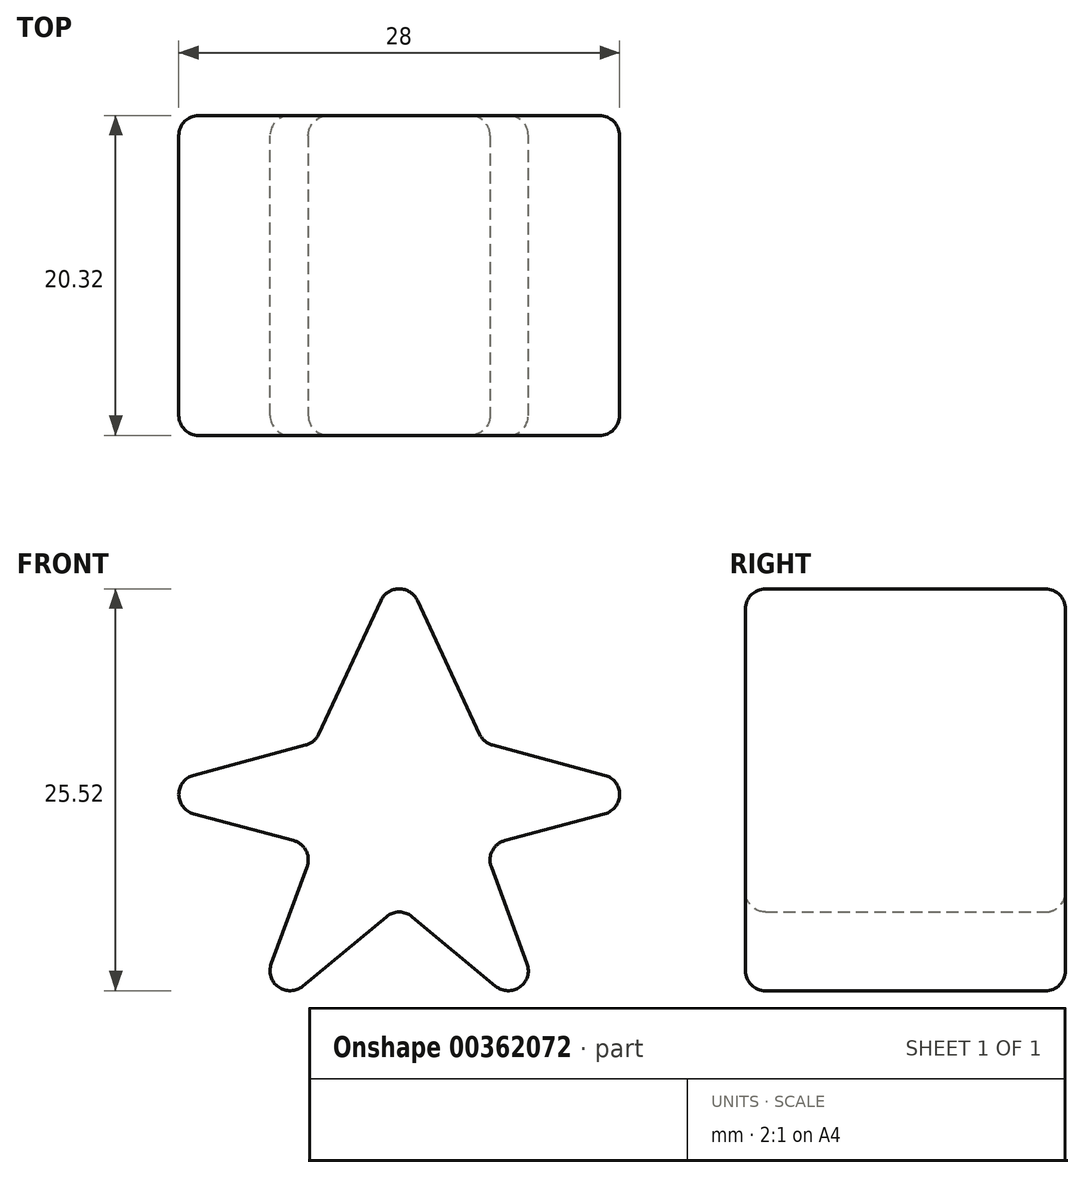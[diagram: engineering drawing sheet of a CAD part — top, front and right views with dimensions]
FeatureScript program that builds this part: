
annotation { "Feature Type Name" : "Feature", "Feature Type Description" : "" }
export const myFeature = defineFeature(function(context is Context, id is Id, definition is map)
    precondition{}
    {
        {
            var Q0;
            Q0=qCreatedBy(makeId("Front.planeOp"),FACE);
            var sketch = newSketch(context, id + "F0", { "sketchPlane" : qUnion([Q0])});
            skLineSegment(sketch, "E0", {"start": v(0, 14.8) * mm, "end": v(-5.37, 3.29) * mm});
            skLineSegment(sketch, "E1", {"start": v(-5.37, 3.29) * mm, "end": v(-17.63, 0) * mm});
            skLineSegment(sketch, "E2", {"start": v(-17.63, 0) * mm, "end": v(-5.37, -3.29) * mm});
            skLineSegment(sketch, "E3", {"start": v(-5.37, -3.29) * mm, "end": v(-9.77, -15.2) * mm});
            skLineSegment(sketch, "E4", {"start": v(-9.77, -15.2) * mm, "end": v(0, -7.08) * mm});
            skLineSegment(sketch, "E5.MirrorCS", {"start": v(0, 14.8) * mm, "end": v(5.37, 3.29) * mm});
            skLineSegment(sketch, "E6.MirrorCS", {"start": v(5.37, 3.29) * mm, "end": v(17.63, 0) * mm});
            skLineSegment(sketch, "E7.MirrorCS", {"start": v(17.63, 0) * mm, "end": v(5.37, -3.29) * mm});
            skLineSegment(sketch, "E8.MirrorCS", {"start": v(5.37, -3.29) * mm, "end": v(9.77, -15.2) * mm});
            skLineSegment(sketch, "E9.MirrorCS", {"start": v(9.77, -15.2) * mm, "end": v(0, -7.08) * mm});
            skSolve(sketch);
        }
        {
            var Q0;
            Q0=makeQuery(id+"F0.imprint","IMPRINT",FACE,{"disambiguationData":[TD([[makeQuery(id+"F0.imprint","IMPRINT",EDGE,{"derivedFrom":sQuery(id+"F0.wireOp",EDGE,"E0")}),1.0]])]});
            extrude(context, id + "F1", {"entities" : qUnion([Q0]), "depth" : 20.32 * mm});
        }
        {
            var Q0;
            Q0=makeQuery(id+"F1.opExtrude","CAP_EDGE",EDGE,{"disambiguationData":[OSD([sQuery(id+"F0.wireOp",EDGE,"E2")])],"isStart":false});
            var Q1;
            Q1=makeQuery(id+"F1.opExtrude","SWEPT_EDGE",EDGE,{"disambiguationData":[OSD([sQuery(id+"F0.wireOp",EDGE,"E0"),sQuery(id+"F0.wireOp",EDGE,"E5.MirrorCS")])]});
            var Q2;
            Q2=makeQuery(id+"F1.opExtrude","SWEPT_EDGE",EDGE,{"disambiguationData":[OSD([sQuery(id+"F0.wireOp",EDGE,"E1"),sQuery(id+"F0.wireOp",EDGE,"E2")])]});
            var Q3;
            Q3=makeQuery(id+"F1.opExtrude","SWEPT_EDGE",EDGE,{"disambiguationData":[OSD([sQuery(id+"F0.wireOp",EDGE,"E6.MirrorCS"),sQuery(id+"F0.wireOp",EDGE,"E7.MirrorCS")])]});
            var Q4;
            Q4=makeQuery(id+"F1.opExtrude","SWEPT_EDGE",EDGE,{"disambiguationData":[OSD([sQuery(id+"F0.wireOp",EDGE,"E8.MirrorCS"),sQuery(id+"F0.wireOp",EDGE,"E9.MirrorCS")])]});
            var Q5;
            Q5=makeQuery(id+"F1.opExtrude","CAP_EDGE",EDGE,{"disambiguationData":[OSD([sQuery(id+"F0.wireOp",EDGE,"E0")])],"isStart":false});
            var Q6;
            Q6=makeQuery(id+"F1.opExtrude","CAP_EDGE",EDGE,{"disambiguationData":[OSD([sQuery(id+"F0.wireOp",EDGE,"E9.MirrorCS")])],"isStart":false});
            var Q7;
            Q7=makeQuery(id+"F1.opExtrude","CAP_EDGE",EDGE,{"disambiguationData":[OSD([sQuery(id+"F0.wireOp",EDGE,"E6.MirrorCS")])],"isStart":false});
            var Q8;
            Q8=makeQuery(id+"F1.opExtrude","CAP_EDGE",EDGE,{"disambiguationData":[OSD([sQuery(id+"F0.wireOp",EDGE,"E8.MirrorCS")])],"isStart":true});
            var Q9;
            Q9=makeQuery(id+"F1.opExtrude","CAP_EDGE",EDGE,{"disambiguationData":[OSD([sQuery(id+"F0.wireOp",EDGE,"E1")])],"isStart":false});
            var Q10;
            Q10=makeQuery(id+"F1.opExtrude","CAP_EDGE",EDGE,{"disambiguationData":[OSD([sQuery(id+"F0.wireOp",EDGE,"E2")])],"isStart":true});
            var Q11;
            Q11=makeQuery(id+"F1.opExtrude","SWEPT_EDGE",EDGE,{"disambiguationData":[OSD([sQuery(id+"F0.wireOp",EDGE,"E0"),sQuery(id+"F0.wireOp",EDGE,"E1")])]});
            var Q12;
            Q12=makeQuery(id+"F1.opExtrude","SWEPT_EDGE",EDGE,{"disambiguationData":[OSD([sQuery(id+"F0.wireOp",EDGE,"E2"),sQuery(id+"F0.wireOp",EDGE,"E3")])]});
            var Q13;
            Q13=makeQuery(id+"F1.opExtrude","SWEPT_EDGE",EDGE,{"disambiguationData":[OSD([sQuery(id+"F0.wireOp",EDGE,"E3"),sQuery(id+"F0.wireOp",EDGE,"E4")])]});
            var Q14;
            Q14=makeQuery(id+"F1.opExtrude","SWEPT_EDGE",EDGE,{"disambiguationData":[OSD([sQuery(id+"F0.wireOp",EDGE,"E4"),sQuery(id+"F0.wireOp",EDGE,"E9.MirrorCS")])]});
            var Q15;
            Q15=makeQuery(id+"F1.opExtrude","SWEPT_EDGE",EDGE,{"disambiguationData":[OSD([sQuery(id+"F0.wireOp",EDGE,"E5.MirrorCS"),sQuery(id+"F0.wireOp",EDGE,"E6.MirrorCS")])]});
            var Q16;
            Q16=makeQuery(id+"F1.opExtrude","SWEPT_EDGE",EDGE,{"disambiguationData":[OSD([sQuery(id+"F0.wireOp",EDGE,"E7.MirrorCS"),sQuery(id+"F0.wireOp",EDGE,"E8.MirrorCS")])]});
            var Q17;
            Q17=makeQuery(id+"F1.opExtrude","CAP_EDGE",EDGE,{"disambiguationData":[OSD([sQuery(id+"F0.wireOp",EDGE,"E0")])],"isStart":true});
            var Q18;
            Q18=makeQuery(id+"F1.opExtrude","CAP_EDGE",EDGE,{"disambiguationData":[OSD([sQuery(id+"F0.wireOp",EDGE,"E1")])],"isStart":true});
            var Q19;
            Q19=makeQuery(id+"F1.opExtrude","CAP_EDGE",EDGE,{"disambiguationData":[OSD([sQuery(id+"F0.wireOp",EDGE,"E3")])],"isStart":true});
            var Q20;
            Q20=makeQuery(id+"F1.opExtrude","CAP_EDGE",EDGE,{"disambiguationData":[OSD([sQuery(id+"F0.wireOp",EDGE,"E3")])],"isStart":false});
            var Q21;
            Q21=makeQuery(id+"F1.opExtrude","CAP_EDGE",EDGE,{"disambiguationData":[OSD([sQuery(id+"F0.wireOp",EDGE,"E5.MirrorCS")])],"isStart":true});
            var Q22;
            Q22=makeQuery(id+"F1.opExtrude","CAP_EDGE",EDGE,{"disambiguationData":[OSD([sQuery(id+"F0.wireOp",EDGE,"E5.MirrorCS")])],"isStart":false});
            var Q23;
            Q23=makeQuery(id+"F1.opExtrude","CAP_EDGE",EDGE,{"disambiguationData":[OSD([sQuery(id+"F0.wireOp",EDGE,"E6.MirrorCS")])],"isStart":true});
            var Q24;
            Q24=makeQuery(id+"F1.opExtrude","CAP_EDGE",EDGE,{"disambiguationData":[OSD([sQuery(id+"F0.wireOp",EDGE,"E7.MirrorCS")])],"isStart":true});
            var Q25;
            Q25=makeQuery(id+"F1.opExtrude","CAP_EDGE",EDGE,{"disambiguationData":[OSD([sQuery(id+"F0.wireOp",EDGE,"E7.MirrorCS")])],"isStart":false});
            var Q26;
            Q26=makeQuery(id+"F1.opExtrude","CAP_EDGE",EDGE,{"disambiguationData":[OSD([sQuery(id+"F0.wireOp",EDGE,"E8.MirrorCS")])],"isStart":false});
            var Q27;
            Q27=makeQuery(id+"F1.opExtrude","CAP_EDGE",EDGE,{"disambiguationData":[OSD([sQuery(id+"F0.wireOp",EDGE,"E4")])],"isStart":true});
            var Q28;
            Q28=makeQuery(id+"F1.opExtrude","CAP_EDGE",EDGE,{"disambiguationData":[OSD([sQuery(id+"F0.wireOp",EDGE,"E4")])],"isStart":false});
            var Q29;
            Q29=makeQuery(id+"F1.opExtrude","CAP_EDGE",EDGE,{"disambiguationData":[OSD([sQuery(id+"F0.wireOp",EDGE,"E9.MirrorCS")])],"isStart":true});
            fillet(context, id + "F2", {"entities" : qUnion([Q0, Q1, Q2, Q3, Q4, Q5, Q6, Q7, Q8, Q9, Q10, Q11, Q12, Q13, Q14, Q15, Q16, Q17, Q18, Q19, Q20, Q21, Q22, Q23, Q24, Q25, Q26, Q27, Q28, Q29]), "radius" : 1.27 * mm, "tangentPropagation" : true, "allowEdgeOverflow" : false});
        }
    });
